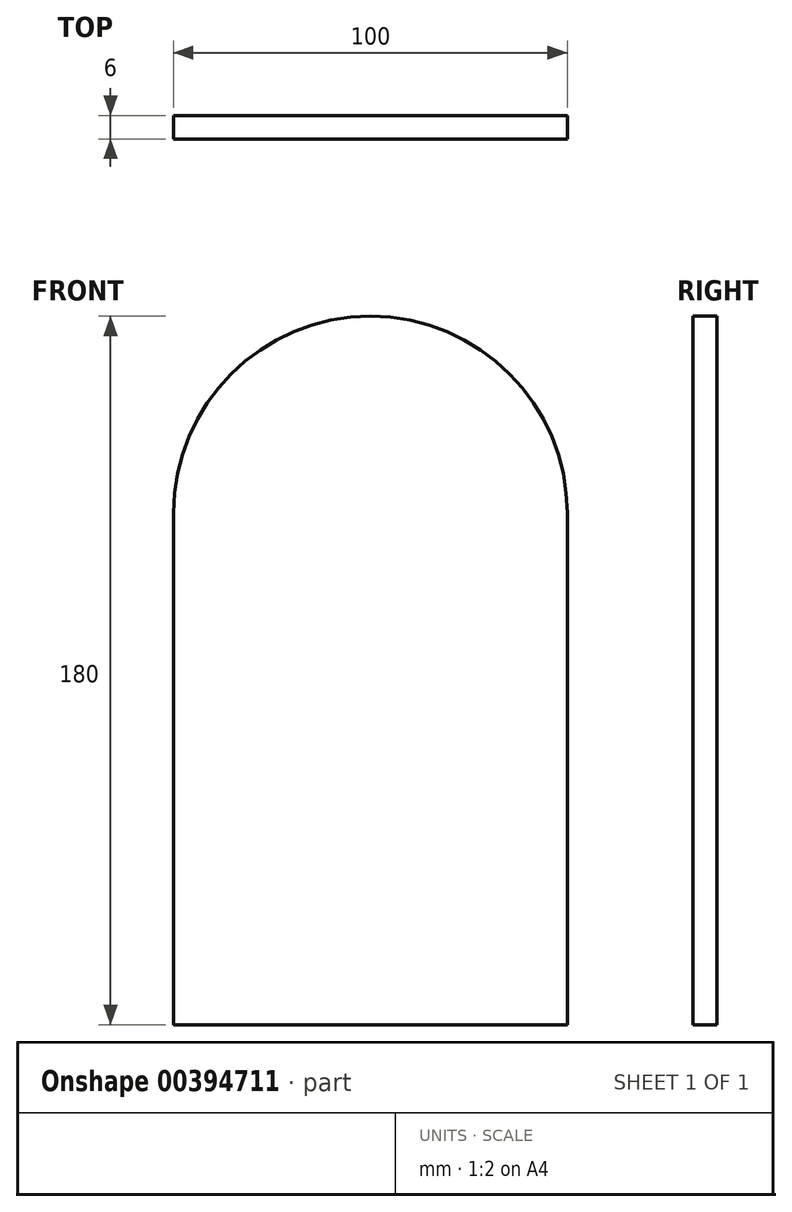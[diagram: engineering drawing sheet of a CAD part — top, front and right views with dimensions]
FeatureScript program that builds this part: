
annotation { "Feature Type Name" : "Feature", "Feature Type Description" : "" }
export const myFeature = defineFeature(function(context is Context, id is Id, definition is map)
    precondition{}
    {
        {
            var Q0;
            Q0=qCreatedBy(makeId("Front.planeOp"),FACE);
            var sketch = newSketch(context, id + "F0", { "sketchPlane" : qUnion([Q0])});
            skLineSegment(sketch, "E0", {"start": v(-50, 0) * mm, "end": v(-50, -130) * mm});
            skLineSegment(sketch, "E1", {"start": v(-50, -130) * mm, "end": v(50, -130) * mm});
            skLineSegment(sketch, "E2", {"start": v(50, -130) * mm, "end": v(50, 0) * mm});
            skArc(sketch, "E3", {"start": v(-50, 0) * mm, "mid": v(0, 50) * mm, "end": v(50, 0) * mm});
            skSolve(sketch);
        }
        {
            var Q0;
            Q0 = qSketchRegion(id + "F0", true);
            extrude(context, id + "F1", {"entities" : qUnion([Q0]), "depth" : 6 * mm});
        }
    });
